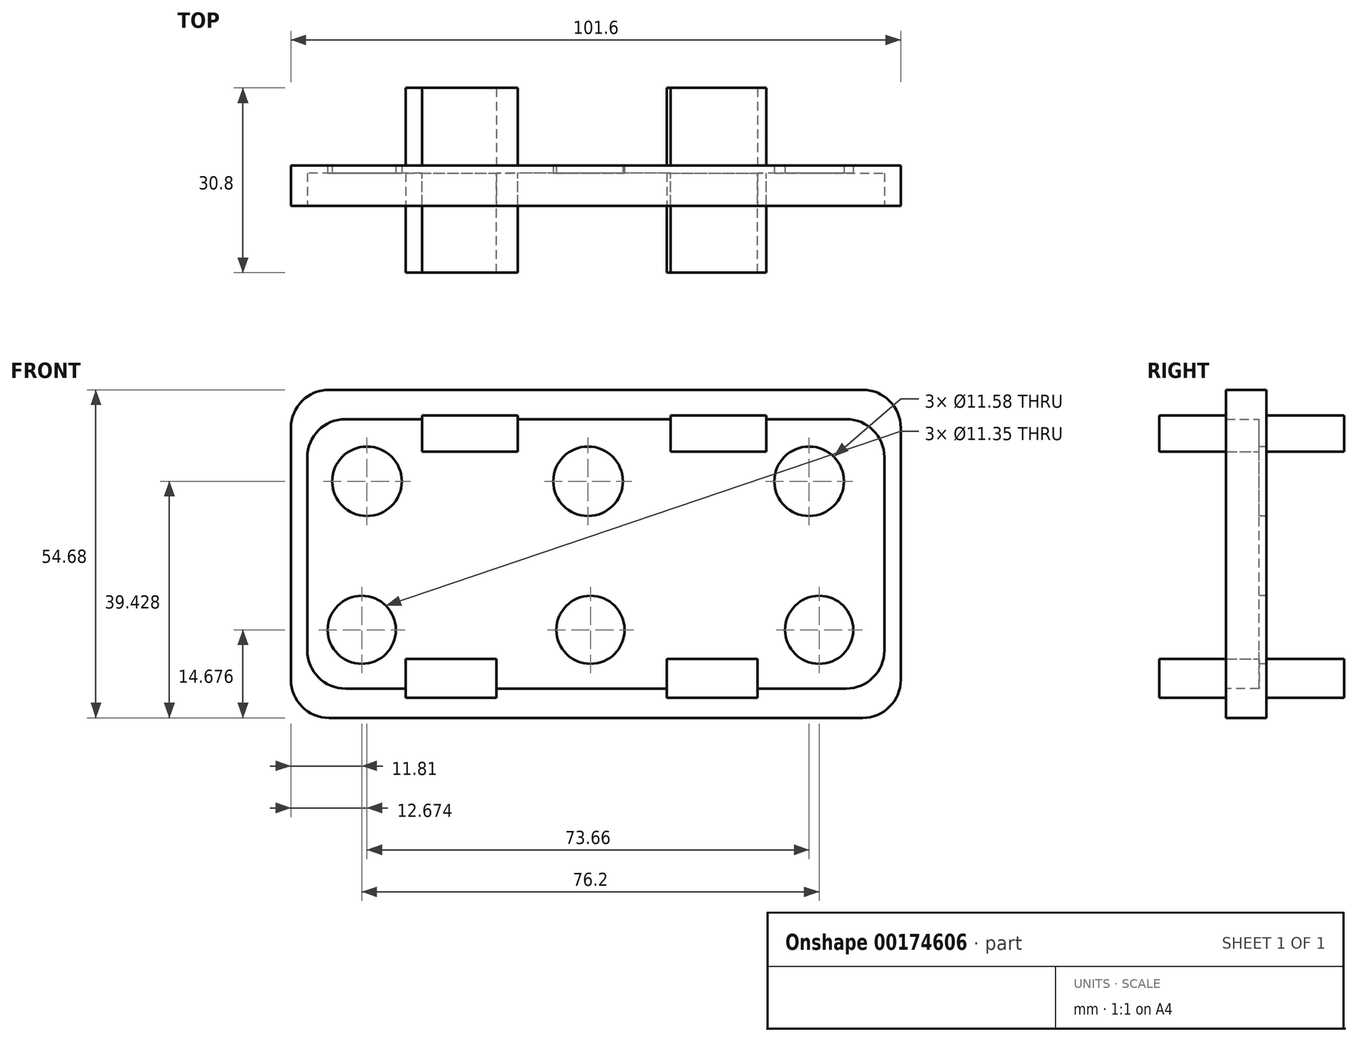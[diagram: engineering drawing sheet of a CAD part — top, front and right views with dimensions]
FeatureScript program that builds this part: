
annotation { "Feature Type Name" : "Feature", "Feature Type Description" : "" }
export const myFeature = defineFeature(function(context is Context, id is Id, definition is map)
    precondition{}
    {
        {
            var Q0;
            Q0=qCreatedBy(makeId("Front.planeOp"),FACE);
            var sketch = newSketch(context, id + "F0", { "sketchPlane" : qUnion([Q0])});
            skLineSegment(sketch, "E0.bottom", {"start": v(-44.45, -27.34) * mm, "end": v(44.45, -27.34) * mm});
            skLineSegment(sketch, "E0.top", {"start": v(-44.45, 27.34) * mm, "end": v(44.45, 27.34) * mm});
            skLineSegment(sketch, "E0.left", {"start": v(-50.8, -21) * mm, "end": v(-50.8, 21) * mm});
            skLineSegment(sketch, "E0.right", {"start": v(50.8, -21) * mm, "end": v(50.8, 21) * mm});
            skPoint(sketch, "E0.middle", {"position": v(0, 0) * mm});
            skPoint(sketch, "E1.visualSharp", {"position": v(-50.8, 27.34) * mm});
            skArc(sketch, "E1.filletArc", {"start": v(-44.45, 27.34) * mm, "mid": v(-48.94, 25.48) * mm, "end": v(-50.8, 21) * mm});
            skPoint(sketch, "E2.visualSharp", {"position": v(50.8, 27.34) * mm});
            skArc(sketch, "E2.filletArc", {"start": v(50.8, 21) * mm, "mid": v(48.94, 25.48) * mm, "end": v(44.45, 27.34) * mm});
            skPoint(sketch, "E3.visualSharp", {"position": v(50.8, -27.34) * mm});
            skArc(sketch, "E3.filletArc", {"start": v(44.45, -27.34) * mm, "mid": v(48.94, -25.48) * mm, "end": v(50.8, -21) * mm});
            skPoint(sketch, "E4.visualSharp", {"position": v(-50.8, -27.34) * mm});
            skArc(sketch, "E4.filletArc", {"start": v(-50.8, -21) * mm, "mid": v(-48.94, -25.48) * mm, "end": v(-44.45, -27.34) * mm});
            skLineSegment(sketch, "E5.bottom", {"start": v(-37.83, -17.84) * mm, "end": v(37.83, -17.84) * mm});
            skLineSegment(sketch, "E5.top", {"start": v(-37.83, 17.84) * mm, "end": v(37.83, 17.84) * mm});
            skLineSegment(sketch, "E5.left", {"start": v(-44.18, -11.5) * mm, "end": v(-44.18, 11.5) * mm});
            skLineSegment(sketch, "E5.right", {"start": v(44.18, -11.5) * mm, "end": v(44.18, 11.5) * mm});
            skPoint(sketch, "E6.visualSharp", {"position": v(-44.18, 17.84) * mm});
            skArc(sketch, "E6.filletArc", {"start": v(-37.83, 17.84) * mm, "mid": v(-42.32, 15.98) * mm, "end": v(-44.18, 11.5) * mm});
            skPoint(sketch, "E7.visualSharp", {"position": v(44.18, 17.84) * mm});
            skArc(sketch, "E7.filletArc", {"start": v(44.18, 11.5) * mm, "mid": v(42.32, 15.98) * mm, "end": v(37.83, 17.84) * mm});
            skPoint(sketch, "E8.visualSharp", {"position": v(44.18, -17.84) * mm});
            skArc(sketch, "E8.filletArc", {"start": v(37.83, -17.84) * mm, "mid": v(42.32, -15.98) * mm, "end": v(44.18, -11.5) * mm});
            skPoint(sketch, "E9.visualSharp", {"position": v(-44.18, -17.84) * mm});
            skArc(sketch, "E9.filletArc", {"start": v(-44.18, -11.5) * mm, "mid": v(-42.32, -15.98) * mm, "end": v(-37.83, -17.84) * mm});
            skSolve(sketch);
        }
        {
            var Q0;
            Q0=makeQuery(id+"F0.imprint","IMPRINT",FACE,{"disambiguationData":[TD([[makeQuery(id+"F0.imprint","IMPRINT",EDGE,{"derivedFrom":sQuery(id+"F0.wireOp",EDGE,"E0.bottom")}),1.0]])]});
            var Q1;
            Q1=makeQuery(id+"F0.imprint","IMPRINT",FACE,{"disambiguationData":[TD([[makeQuery(id+"F0.imprint","IMPRINT",EDGE,{"derivedFrom":sQuery(id+"F0.wireOp",EDGE,"E5.bottom")}),1.0]])]});
            extrude(context, id + "F1", {"entities" : qUnion([Q0, Q1]), "oppositeDirection" : true, "depth" : 22.86 * mm});
        }
        {
            var Q0;
            Q0=qCreatedBy(makeId("Front.planeOp"),FACE);
            var sketch = newSketch(context, id + "F2", { "sketchPlane" : qUnion([Q0])});
            skLineSegment(sketch, "E10.bottom", {"start": v(41.71, -22.45) * mm, "end": v(-41.71, -22.45) * mm});
            skLineSegment(sketch, "E10.top", {"start": v(41.71, 22.45) * mm, "end": v(-41.71, 22.45) * mm});
            skLineSegment(sketch, "E10.left", {"start": v(48.06, -16.1) * mm, "end": v(48.06, 16.1) * mm});
            skLineSegment(sketch, "E10.right", {"start": v(-48.06, -16.1) * mm, "end": v(-48.06, 16.1) * mm});
            skPoint(sketch, "E10.middle", {"position": v(0, 0) * mm});
            skPoint(sketch, "E11.visualSharp", {"position": v(48.06, 22.45) * mm});
            skArc(sketch, "E11.filletArc", {"start": v(48.06, 16.1) * mm, "mid": v(46.2, 20.59) * mm, "end": v(41.71, 22.45) * mm});
            skPoint(sketch, "E12.visualSharp", {"position": v(-48.06, 22.45) * mm});
            skArc(sketch, "E12.filletArc", {"start": v(-41.71, 22.45) * mm, "mid": v(-46.2, 20.59) * mm, "end": v(-48.06, 16.1) * mm});
            skPoint(sketch, "E13.visualSharp", {"position": v(48.06, -22.45) * mm});
            skArc(sketch, "E13.filletArc", {"start": v(41.71, -22.45) * mm, "mid": v(46.2, -20.59) * mm, "end": v(48.06, -16.1) * mm});
            skPoint(sketch, "E14.visualSharp", {"position": v(-48.06, -22.45) * mm});
            skArc(sketch, "E14.filletArc", {"start": v(-48.06, -16.1) * mm, "mid": v(-46.2, -20.59) * mm, "end": v(-41.71, -22.45) * mm});
            skSolve(sketch);
        }
        {
            var Q0;
            Q0=makeQuery(id+"F2.imprint","IMPRINT",FACE,{"disambiguationData":[TD([[makeQuery(id+"F2.imprint","IMPRINT",EDGE,{"derivedFrom":sQuery(id+"F2.wireOp",EDGE,"E10.bottom")}),-1.0]])]});
            extrude(context, id + "F3", {"entities" : qUnion([Q0]), "operationType" : NewBodyOperationType.REMOVE, "oppositeDirection" : true, "depth" : 21.59 * mm});
        }
        {
            var Q0;
            Q0=makeQuery(id+"F3.boolean.opBoolean","COPY",FACE,{"derivedFrom":makeQuery(id+"F3.opExtrude","CAP_FACE",FACE,{"disambiguationData":[OSD([sQuery(id+"F2.wireOp",EDGE,"E10.bottom"),sQuery(id+"F2.wireOp",EDGE,"E10.top"),sQuery(id+"F2.wireOp",EDGE,"E10.left"),sQuery(id+"F2.wireOp",EDGE,"E10.right"),sQuery(id+"F2.wireOp",EDGE,"E11.filletArc"),sQuery(id+"F2.wireOp",EDGE,"E12.filletArc"),sQuery(id+"F2.wireOp",EDGE,"E13.filletArc"),sQuery(id+"F2.wireOp",EDGE,"E14.filletArc")])],"isStart":false})});
            var sketch = newSketch(context, id + "F4", { "sketchPlane" : qUnion([Q0])});
            skCircle(sketch, "E15", {"center": v(-38.13, 12.09) * mm, "radius": 5.8 * mm});
            skCircle(sketch, "E16.1.0.0", {"center": v(-1.3, 12.09) * mm, "radius": 5.8 * mm});
            skCircle(sketch, "E16.2.0.0", {"center": v(35.53, 12.09) * mm, "radius": 5.8 * mm});
            skLineSegment(sketch, "E16.direction1", {"start": v(-38.13, 12.09) * mm, "end": v(-1.3, 12.09) * mm, "construction": true});
            skCircle(sketch, "E17", {"center": v(-38.99, -12.66) * mm, "radius": 5.68 * mm});
            skCircle(sketch, "E18.1.0.0", {"center": v(-0.89, -12.66) * mm, "radius": 5.68 * mm});
            skCircle(sketch, "E18.2.0.0", {"center": v(37.21, -12.66) * mm, "radius": 5.68 * mm});
            skLineSegment(sketch, "E18.direction1", {"start": v(-38.99, -12.66) * mm, "end": v(-0.89, -12.66) * mm, "construction": true});
            skSolve(sketch);
        }
        {
            var Q0;
            Q0=makeQuery(id+"F4.imprint","IMPRINT",FACE,{"disambiguationData":[TD([[makeQuery(id+"F4.imprint","IMPRINT",EDGE,{"derivedFrom":sQuery(id+"F4.wireOp",EDGE,"E15")}),1.0]])]});
            var Q1;
            Q1=makeQuery(id+"F4.imprint","IMPRINT",FACE,{"disambiguationData":[TD([[makeQuery(id+"F4.imprint","IMPRINT",EDGE,{"derivedFrom":sQuery(id+"F4.wireOp",EDGE,"E16.1.0.0")}),1.0]])]});
            var Q2;
            Q2=makeQuery(id+"F4.imprint","IMPRINT",FACE,{"disambiguationData":[TD([[makeQuery(id+"F4.imprint","IMPRINT",EDGE,{"derivedFrom":sQuery(id+"F4.wireOp",EDGE,"E16.2.0.0")}),1.0]])]});
            var Q3;
            Q3=makeQuery(id+"F4.imprint","IMPRINT",FACE,{"disambiguationData":[TD([[makeQuery(id+"F4.imprint","IMPRINT",EDGE,{"derivedFrom":sQuery(id+"F4.wireOp",EDGE,"E17")}),1.0]])]});
            var Q4;
            Q4=makeQuery(id+"F4.imprint","IMPRINT",FACE,{"disambiguationData":[TD([[makeQuery(id+"F4.imprint","IMPRINT",EDGE,{"derivedFrom":sQuery(id+"F4.wireOp",EDGE,"E18.1.0.0")}),1.0]])]});
            var Q5;
            Q5=makeQuery(id+"F4.imprint","IMPRINT",FACE,{"disambiguationData":[TD([[makeQuery(id+"F4.imprint","IMPRINT",EDGE,{"derivedFrom":sQuery(id+"F4.wireOp",EDGE,"E18.2.0.0")}),1.0]])]});
            extrude(context, id + "F5", {"entities" : qUnion([Q0, Q1, Q2, Q3, Q4, Q5]), "operationType" : NewBodyOperationType.REMOVE, "oppositeDirection" : true, "depth" : 25.4 * mm});
        }
        {
            var Q0;
            Q0=makeQuery(id+"F1.opExtrude","CAP_FACE",FACE,{"disambiguationData":[OSD([sQuery(id+"F0.wireOp",EDGE,"E0.bottom"),sQuery(id+"F0.wireOp",EDGE,"E0.top"),sQuery(id+"F0.wireOp",EDGE,"E0.left"),sQuery(id+"F0.wireOp",EDGE,"E0.right"),sQuery(id+"F0.wireOp",EDGE,"E1.filletArc"),sQuery(id+"F0.wireOp",EDGE,"E2.filletArc"),sQuery(id+"F0.wireOp",EDGE,"E3.filletArc"),sQuery(id+"F0.wireOp",EDGE,"E4.filletArc")])],"isStart":false});
            var sketch = newSketch(context, id + "F6", { "sketchPlane" : qUnion([Q0])});
            skLineSegment(sketch, "E19.bottom", {"start": v(-28.43, 23.03) * mm, "end": v(-12.47, 23.03) * mm});
            skLineSegment(sketch, "E19.top", {"start": v(-28.43, 17) * mm, "end": v(-12.47, 17) * mm});
            skLineSegment(sketch, "E19.left", {"start": v(-28.43, 23.03) * mm, "end": v(-28.43, 17) * mm});
            skLineSegment(sketch, "E19.right", {"start": v(-12.47, 23.03) * mm, "end": v(-12.47, 17) * mm});
            skLineSegment(sketch, "E20.1.0.0", {"start": v(12.97, 23.03) * mm, "end": v(28.93, 23.03) * mm});
            skLineSegment(sketch, "E20.1.0.1", {"start": v(28.93, 23.03) * mm, "end": v(28.93, 17) * mm});
            skLineSegment(sketch, "E20.1.0.2", {"start": v(12.97, 17) * mm, "end": v(28.93, 17) * mm});
            skLineSegment(sketch, "E20.1.0.3", {"start": v(12.97, 23.03) * mm, "end": v(12.97, 17) * mm});
            skLineSegment(sketch, "E20.direction1", {"start": v(-28.43, 23.03) * mm, "end": v(12.97, 23.03) * mm, "construction": true});
            skLineSegment(sketch, "E21.bottom", {"start": v(-26.92, -23.97) * mm, "end": v(-11.82, -23.97) * mm});
            skLineSegment(sketch, "E21.top", {"start": v(-26.92, -17.5) * mm, "end": v(-11.82, -17.5) * mm});
            skLineSegment(sketch, "E21.left", {"start": v(-26.92, -23.97) * mm, "end": v(-26.92, -17.5) * mm});
            skLineSegment(sketch, "E21.right", {"start": v(-11.82, -23.97) * mm, "end": v(-11.82, -17.5) * mm});
            skPoint(sketch, "E21.middle", {"position": v(-19.37, -20.73) * mm});
            skLineSegment(sketch, "E22.1.0.0", {"start": v(16.58, -17.5) * mm, "end": v(31.68, -17.5) * mm});
            skLineSegment(sketch, "E22.1.0.1", {"start": v(31.68, -23.97) * mm, "end": v(31.68, -17.5) * mm});
            skLineSegment(sketch, "E22.1.0.2", {"start": v(16.58, -23.97) * mm, "end": v(31.68, -23.97) * mm});
            skLineSegment(sketch, "E22.1.0.3", {"start": v(16.58, -23.97) * mm, "end": v(16.58, -17.5) * mm});
            skLineSegment(sketch, "E22.direction1", {"start": v(-26.92, -17.5) * mm, "end": v(16.58, -17.5) * mm, "construction": true});
            skSolve(sketch);
        }
        {
            var Q0;
            Q0=makeQuery(id+"F6.imprint","IMPRINT",FACE,{"disambiguationData":[TD([[makeQuery(id+"F6.imprint","IMPRINT",EDGE,{"derivedFrom":sQuery(id+"F6.wireOp",EDGE,"E19.bottom")}),-1.0]])]});
            var Q1;
            Q1=makeQuery(id+"F6.imprint","IMPRINT",FACE,{"disambiguationData":[TD([[makeQuery(id+"F6.imprint","IMPRINT",EDGE,{"derivedFrom":sQuery(id+"F6.wireOp",EDGE,"E20.1.0.0")}),-1.0]])]});
            var Q2;
            Q2=makeQuery(id+"F6.imprint","IMPRINT",FACE,{"disambiguationData":[TD([[makeQuery(id+"F6.imprint","IMPRINT",EDGE,{"derivedFrom":sQuery(id+"F6.wireOp",EDGE,"E21.bottom")}),1.0]])]});
            var Q3;
            Q3=makeQuery(id+"F6.imprint","IMPRINT",FACE,{"disambiguationData":[TD([[makeQuery(id+"F6.imprint","IMPRINT",EDGE,{"derivedFrom":sQuery(id+"F6.wireOp",EDGE,"E22.1.0.0")}),-1.0]])]});
            extrude(context, id + "F7", {"entities" : qUnion([Q0, Q1, Q2, Q3]), "operationType" : NewBodyOperationType.ADD, "depth" : 12.9 * mm});
        }
        {
            var Q0;
            Q0=makeQuery(id+"F1.opExtrude","CAP_FACE",FACE,{"disambiguationData":[OSD([sQuery(id+"F0.wireOp",EDGE,"E0.bottom"),sQuery(id+"F0.wireOp",EDGE,"E0.top"),sQuery(id+"F0.wireOp",EDGE,"E0.left"),sQuery(id+"F0.wireOp",EDGE,"E0.right"),sQuery(id+"F0.wireOp",EDGE,"E1.filletArc"),sQuery(id+"F0.wireOp",EDGE,"E2.filletArc"),sQuery(id+"F0.wireOp",EDGE,"E3.filletArc"),sQuery(id+"F0.wireOp",EDGE,"E4.filletArc")])],"isStart":true});
            extrude(context, id + "F8", {"entities" : qUnion([Q0]), "operationType" : NewBodyOperationType.REMOVE, "oppositeDirection" : true, "depth" : 16.1 * mm});
        }
        {
            var Q0;
            Q0=makeQuery(id+"F7.opExtrude","CAP_FACE",FACE,{"disambiguationData":[OSD([sQuery(id+"F6.wireOp",EDGE,"E19.bottom"),sQuery(id+"F6.wireOp",EDGE,"E19.top"),sQuery(id+"F6.wireOp",EDGE,"E19.left"),sQuery(id+"F6.wireOp",EDGE,"E19.right")])],"isStart":false});
            var Q1;
            Q1=makeQuery(id+"F7.opExtrude","CAP_FACE",FACE,{"disambiguationData":[OSD([sQuery(id+"F6.wireOp",EDGE,"E20.1.0.0"),sQuery(id+"F6.wireOp",EDGE,"E20.1.0.1"),sQuery(id+"F6.wireOp",EDGE,"E20.1.0.2"),sQuery(id+"F6.wireOp",EDGE,"E20.1.0.3")])],"isStart":false});
            var Q2;
            Q2=makeQuery(id+"F7.opExtrude","CAP_FACE",FACE,{"disambiguationData":[OSD([sQuery(id+"F6.wireOp",EDGE,"E22.1.0.0"),sQuery(id+"F6.wireOp",EDGE,"E22.1.0.1"),sQuery(id+"F6.wireOp",EDGE,"E22.1.0.2"),sQuery(id+"F6.wireOp",EDGE,"E22.1.0.3")])],"isStart":false});
            var Q3;
            Q3=makeQuery(id+"F7.opExtrude","CAP_FACE",FACE,{"disambiguationData":[OSD([sQuery(id+"F6.wireOp",EDGE,"E21.bottom"),sQuery(id+"F6.wireOp",EDGE,"E21.top"),sQuery(id+"F6.wireOp",EDGE,"E21.left"),sQuery(id+"F6.wireOp",EDGE,"E21.right")])],"isStart":false});
            extrude(context, id + "F9", {"entities" : qUnion([Q0, Q1, Q2, Q3]), "operationType" : NewBodyOperationType.ADD, "oppositeDirection" : true, "depth" : 30.8 * mm});
        }
    });
